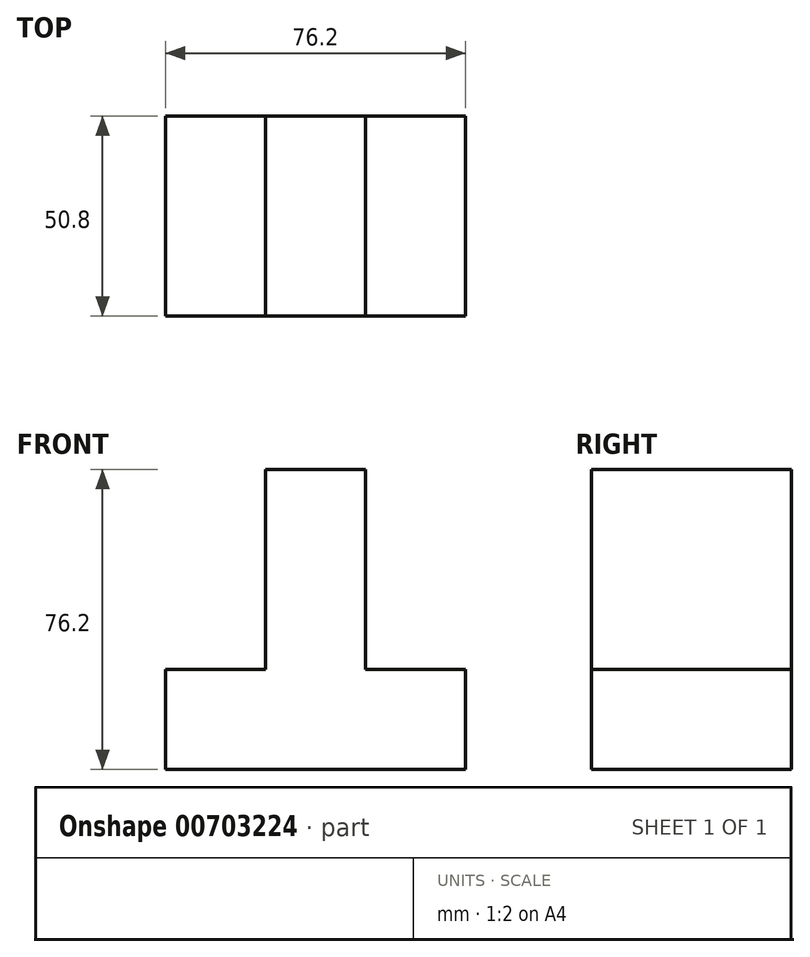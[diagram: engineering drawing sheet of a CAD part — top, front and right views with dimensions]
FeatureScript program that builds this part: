
annotation { "Feature Type Name" : "Feature", "Feature Type Description" : "" }
export const myFeature = defineFeature(function(context is Context, id is Id, definition is map)
    precondition{}
    {
        {
            var Q0;
            Q0=qCreatedBy(makeId("Front.planeOp"),FACE);
            var sketch = newSketch(context, id + "F0", { "sketchPlane" : qUnion([Q0])});
            skLineSegment(sketch, "E0", {"start": v(42.69, -16.9) * mm, "end": v(-33.51, -16.9) * mm});
            skLineSegment(sketch, "E1", {"start": v(-33.51, -16.9) * mm, "end": v(-33.51, 8.5) * mm});
            skLineSegment(sketch, "E2", {"start": v(-33.51, 8.5) * mm, "end": v(-8.11, 8.5) * mm});
            skLineSegment(sketch, "E3", {"start": v(-8.11, 8.5) * mm, "end": v(-8.11, 59.3) * mm});
            skLineSegment(sketch, "E4", {"start": v(-8.11, 59.3) * mm, "end": v(17.29, 59.3) * mm});
            skLineSegment(sketch, "E5", {"start": v(17.29, 8.5) * mm, "end": v(42.69, 8.5) * mm});
            skLineSegment(sketch, "E6", {"start": v(42.69, 8.5) * mm, "end": v(42.69, -16.9) * mm});
            skLineSegment(sketch, "E7", {"start": v(17.29, 59.3) * mm, "end": v(17.29, 8.5) * mm});
            skSolve(sketch);
        }
        {
            var Q0;
            Q0 = qSketchRegion(id + "F0", true);
            extrude(context, id + "F1", {"entities" : qUnion([Q0]), "depth" : 50.8 * mm, "offsetDistance" : 25.4 * mm});
        }
    });
